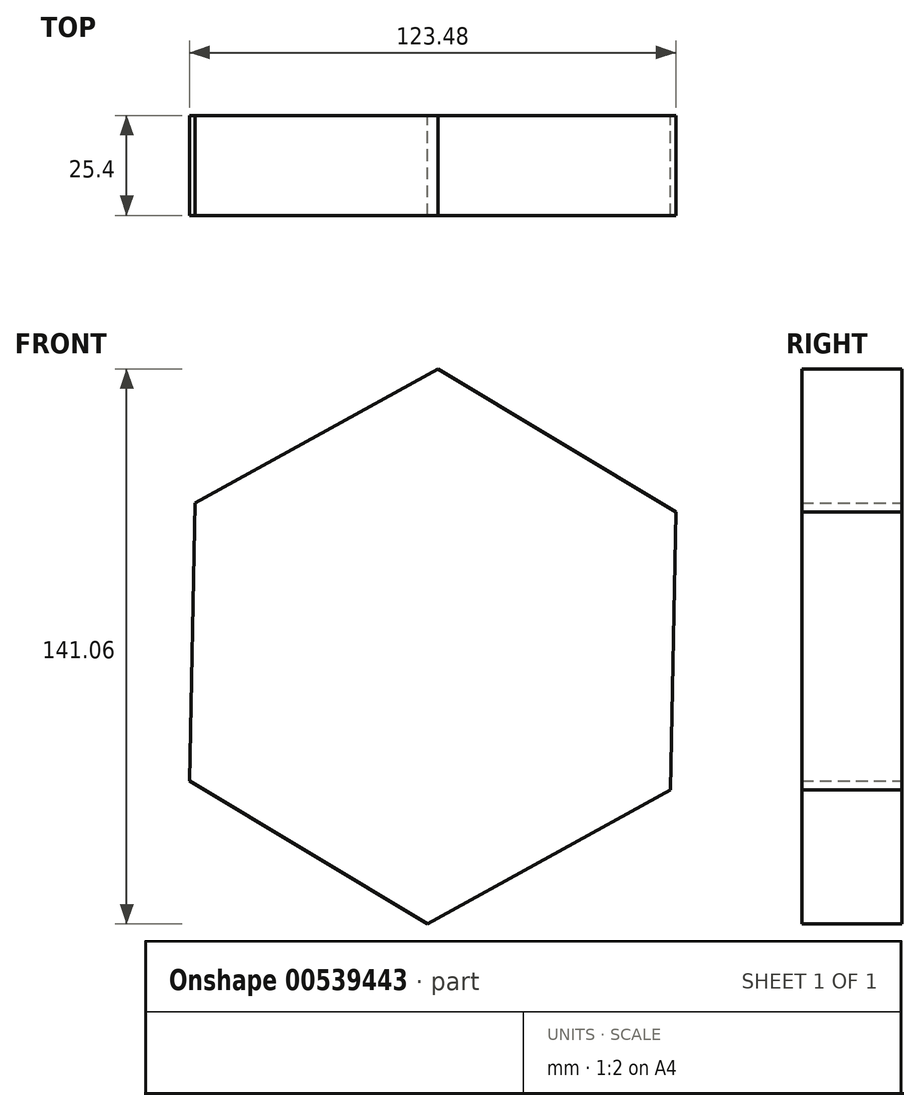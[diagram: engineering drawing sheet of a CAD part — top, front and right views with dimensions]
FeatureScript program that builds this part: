
annotation { "Feature Type Name" : "Feature", "Feature Type Description" : "" }
export const myFeature = defineFeature(function(context is Context, id is Id, definition is map)
    precondition{}
    {
        {
            var Q0;
            Q0=qCreatedBy(makeId("Front.planeOp"),FACE);
            var sketch = newSketch(context, id + "F0", { "sketchPlane" : qUnion([Q0])});
            skCircle(sketch, "E0.cCircle", {"center": v(0, 0) * mm, "radius": 61.09 * mm, "construction": true});
            skLineSegment(sketch, "E0.0", {"start": v(60.42, -36.4) * mm, "end": v(-1.32, -70.53) * mm});
            skLineSegment(sketch, "E0.1", {"start": v(-1.32, -70.53) * mm, "end": v(-61.74, -34.12) * mm});
            skLineSegment(sketch, "E0.2", {"start": v(-61.74, -34.12) * mm, "end": v(-60.42, 36.4) * mm});
            skLineSegment(sketch, "E0.3", {"start": v(-60.42, 36.4) * mm, "end": v(1.32, 70.53) * mm});
            skLineSegment(sketch, "E0.4", {"start": v(1.32, 70.53) * mm, "end": v(61.74, 34.12) * mm});
            skLineSegment(sketch, "E0.5", {"start": v(61.74, 34.12) * mm, "end": v(60.42, -36.4) * mm});
            skPoint(sketch, "E0.0.midPoint", {"position": v(29.55, -53.47) * mm});
            skSolve(sketch);
        }
        {
            var Q0;
            Q0=makeQuery(id+"F0.imprint","IMPRINT",FACE,{"disambiguationData":[TD([[makeQuery(id+"F0.imprint","IMPRINT",EDGE,{"derivedFrom":sQuery(id+"F0.wireOp",EDGE,"E0.0")}),-1.0]])]});
            extrude(context, id + "F1", {"entities" : qUnion([Q0]), "depth" : 25.4 * mm, "offsetDistance" : 25.4 * mm});
        }
    });
